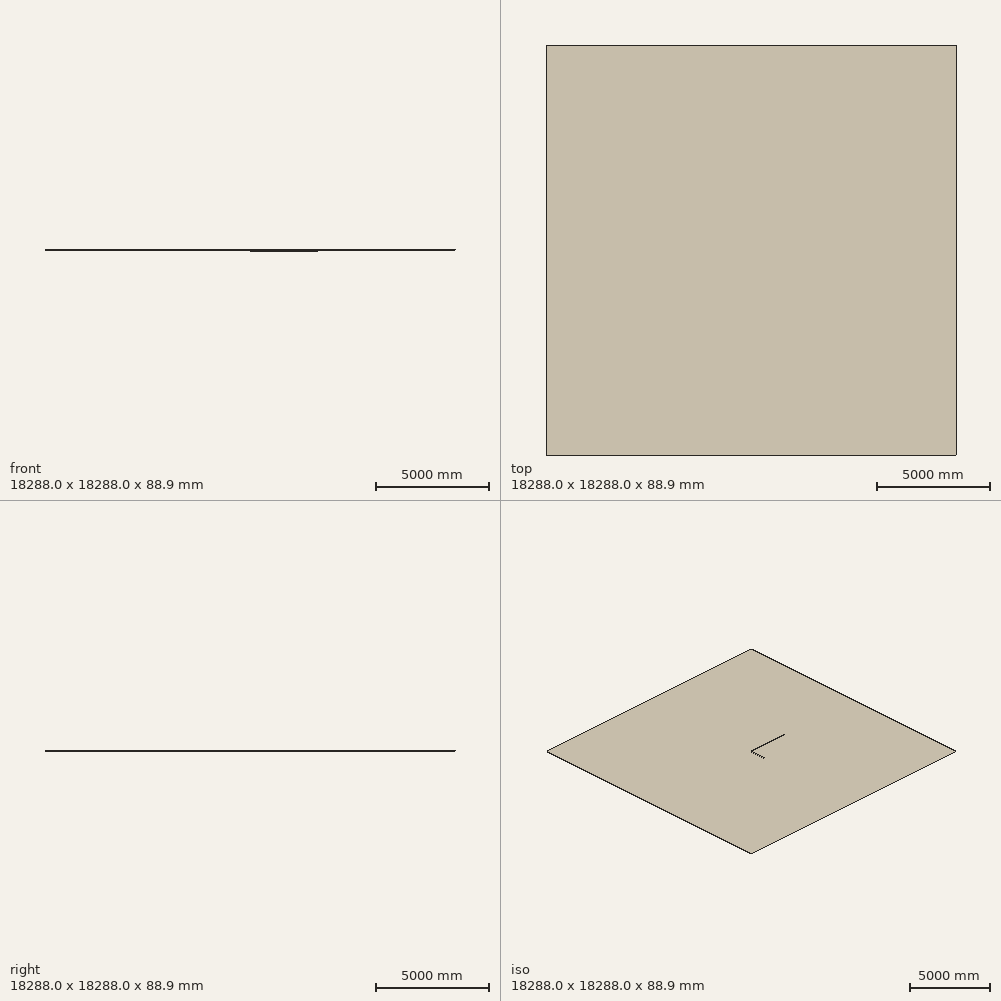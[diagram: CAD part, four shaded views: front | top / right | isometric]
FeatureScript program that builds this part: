
annotation { "Feature Type Name" : "Feature", "Feature Type Description" : "" }
export const myFeature = defineFeature(function(context is Context, id is Id, definition is map)
    precondition{}
    {
        {
            var Q0;
            Q0=qCreatedBy(makeId("Right.planeOp"),FACE);
            var sketch = newSketch(context, id + "F0", { "sketchPlane" : qUnion([Q0])});
            skLineSegment(sketch, "E0.bottom", {"start": v(-14.03, 27.43) * mm, "end": v(-5.43, 27.43) * mm});
            skLineSegment(sketch, "E0.top", {"start": v(-14.03, 18.41) * mm, "end": v(-5.43, 18.41) * mm});
            skLineSegment(sketch, "E0.left", {"start": v(-14.03, 27.43) * mm, "end": v(-14.03, 18.41) * mm});
            skLineSegment(sketch, "E0.right", {"start": v(-5.43, 27.43) * mm, "end": v(-5.43, 18.41) * mm});
            skSolve(sketch);
        }
        {
            var Q0;
            Q0 = qSketchRegion(id + "F0", true);
            extrude(context, id + "F1", {"entities" : qUnion([Q0]), "endBound" : BoundingType.SYMMETRIC, "depth" : 990.6 * mm});
        }
        {
            var Q0;
            Q0=qCreatedBy(makeId("Top.planeOp"),FACE);
            var sketch = newSketch(context, id + "F2", { "sketchPlane" : qUnion([Q0])});
            skLineSegment(sketch, "E1.bottom", {"start": v(9144, -9144) * mm, "end": v(-9144, -9144) * mm});
            skLineSegment(sketch, "E1.top", {"start": v(9144, 9144) * mm, "end": v(-9144, 9144) * mm});
            skLineSegment(sketch, "E1.left", {"start": v(9144, -9144) * mm, "end": v(9144, 9144) * mm});
            skLineSegment(sketch, "E1.right", {"start": v(-9144, -9144) * mm, "end": v(-9144, 9144) * mm});
            skPoint(sketch, "E1.middle", {"position": v(0, 0) * mm});
            skSolve(sketch);
        }
        {
            var Q0;
            Q0 = qSketchRegion(id + "F2", true);
            extrude(context, id + "F3", {"entities" : qUnion([Q0]), "depth" : 25.4 * mm});
        }
        {
            var Q0;
            Q0 = qSketchRegion(id + "F0", true);
            extrude(context, id + "F4", {"entities" : qUnion([Q0]), "depth" : 609.6 * mm});
        }
        {
            var Q0;
            Q0 = qSketchRegion(id + "F0", true);
            extrude(context, id + "F5", {"entities" : qUnion([Q0]), "depth" : 990.6 * mm});
        }
        {
            var Q0;
            Q0 = qSketchRegion(id + "F0", true);
            extrude(context, id + "F6", {"entities" : qUnion([Q0]), "depth" : 304.8 * mm});
        }
        {
            var Q0;
            Q0 = qSketchRegion(id + "F0", true);
            extrude(context, id + "F7", {"entities" : qUnion([Q0]), "depth" : 1219.2 * mm});
        }
        {
            var Q0;
            Q0=qCreatedBy(makeId("Front.planeOp"),FACE);
            var sketch = newSketch(context, id + "F8", { "sketchPlane" : qUnion([Q0])});
            skLineSegment(sketch, "E2.bottom", {"start": v(-55.02, 42.9) * mm, "end": v(-39.8, 42.9) * mm});
            skLineSegment(sketch, "E2.top", {"start": v(-55.02, 25.91) * mm, "end": v(-39.8, 25.91) * mm});
            skLineSegment(sketch, "E2.left", {"start": v(-55.02, 42.9) * mm, "end": v(-55.02, 25.91) * mm});
            skLineSegment(sketch, "E2.right", {"start": v(-39.8, 42.9) * mm, "end": v(-39.8, 25.91) * mm});
            skSolve(sketch);
        }
        {
            var Q0;
            Q0 = qSketchRegion(id + "F8", true);
            extrude(context, id + "F9", {"entities" : qUnion([Q0]), "depth" : 1219.2 * mm});
        }
        {
            var Q0;
            Q0=qCreatedBy(makeId("Right.planeOp"),FACE);
            var sketch = newSketch(context, id + "F10", { "sketchPlane" : qUnion([Q0])});
            skLineSegment(sketch, "E3.bottom", {"start": v(19.05, -44.45) * mm, "end": v(-19.05, -44.45) * mm});
            skLineSegment(sketch, "E3.top", {"start": v(19.05, 44.45) * mm, "end": v(-19.05, 44.45) * mm});
            skLineSegment(sketch, "E3.left", {"start": v(19.05, -44.45) * mm, "end": v(19.05, 44.45) * mm});
            skLineSegment(sketch, "E3.right", {"start": v(-19.05, -44.45) * mm, "end": v(-19.05, 44.45) * mm});
            skPoint(sketch, "E3.middle", {"position": v(0, 0) * mm});
            skSolve(sketch);
        }
        {
            var Q0;
            Q0 = qSketchRegion(id + "F10", true);
            extrude(context, id + "F11", {"entities" : qUnion([Q0]), "depth" : 3048 * mm});
        }
    });
